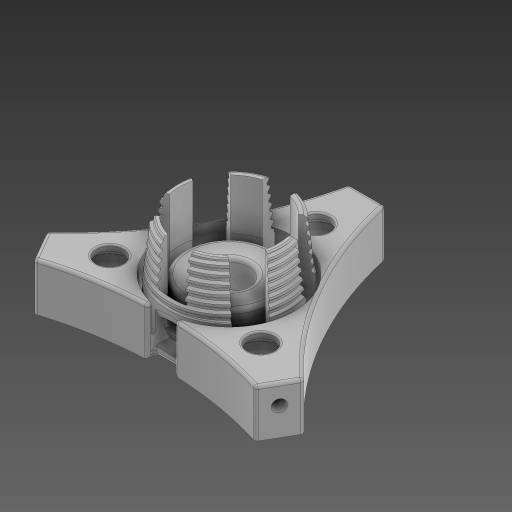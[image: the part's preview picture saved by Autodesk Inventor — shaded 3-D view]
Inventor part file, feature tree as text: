
AUTODESK INVENTOR PART (.ipt)
format: ipt  version: 2024 (Build 280153000, 153)  size: 1,730,560 bytes
history: native  units: mm
features: sketch x17, extrude x12, fillet x9, chamfer x3, hole x3, draft x2, helix x2, plane x2, pattern_circular x2, projected_geometry x2
ambient origin geometry x8: Origin, YZ Plane, XZ Plane, XY Plane, X Axis, Y Axis, Z Axis, Center Point
bodies: Solid1 (feature_tree)
feature tree (54):
  extrude  "Extrusion1"  Depth=29.5mm
  draft  "FaceDraft1"
  sketch  "Sketch2"  dims[d7=6.806784mm d8=0.55605mm]
  helix  "Coil1"  [1 undecoded]
  helix  "Coil2"  [1 undecoded]
  extrude  "Extrusion2"  Depth=0.55605mm
  extrude  "Extrusion3"  TaperAngle=0.0deg  [1 undecoded]
  fillet  "Fillet1"  [1 undecoded]
  chamfer  "Chamfer1"  Distance=0.3mm Angle=45.0deg
  plane  "Work Plane1"
  extrude  "Extrusion4"  TaperAngle=0.0deg  [1 undecoded]
  extrude  "Extrusion8"  Depth=60.0mm TaperAngle=360.0deg
  hole  "Hole2"  [1 undecoded]
  sketch  "Sketch13"  dims[d58=6.0mm d65=60.0mm d67=360.0deg]
  extrude  "Extrusion11"  Depth=10.0mm TaperAngle=0.0deg
  hole  "Bearing Hole"  [1 undecoded]
  pattern_circular  "Circular Pattern4"  Count=3 Angle=360.0deg
  extrude  "Extrusion13"  Depth=7.0mm TaperAngle=0.0deg
  sketch  "Sketch20"  dims[d126=6.804mm d127=6.0mm d128=9.979mm d129=8.89mm d130=90.0deg d131=8.0mm d132=20.594885mm d133=22.0mm d134=30.0mm d135=360.0deg]
  extrude  "Extrusion14"  Depth=1.55mm TaperAngle=45.0deg
  sketch  "Sketch18"  dims[d124=34.0mm]
  fillet  "Fillet9"  Radius=0.24mm
  chamfer  "Chamfer4"  [1 undecoded]
  chamfer  "Chamfer5"  Distance=0.5mm
  fillet  "Fillet11"  Radius=2.0mm
  draft  "FaceDraft2"
  fillet  "Fillet13"  Radius=34.767mm
  extrude  "Extrusion15"  Depth=0.5mm
  hole  "Hole5"  [1 undecoded]
  pattern_circular  "Circular Pattern5"  [2 undecoded]
  plane  "Work Plane4"
  extrude  "Extrusion16"  Depth=0.5mm
  fillet  "Fillet14"  Radius=30.0mm
  fillet  "Fillet16"  Radius=16.0mm
  extrude  "Extrusion17"  TaperAngle=0.0deg  [1 undecoded]
  extrude  "Extrusion19"  Depth=0.5mm
  fillet  "Fillet17"  Radius=0.4mm
  fillet  "Fillet18"  Radius=25.0mm
  fillet  "Fillet19"  Radius=22.0mm
  sketch  "Sketch1"  dims[d0=24.8mm d1=29.5mm d2=12.875mm d3=0.0mm d4=1.047198mm]
  projected_geometry  "Projected Loop1"
  sketch  "Sketch3"  dims[d9=6.806784mm]
  sketch  "Sketch4"  dims[d10=2.0mm d11=10.0mm d12=70.0mm d13=-1.047198mm d14=90.0deg d15=90.0deg d16=0.0mm d17=0.0mm d18=0.6mm]
  sketch  "Sketch5"  dims[d19=2.0mm d20=10.0mm d21=10.0mm d22=1.047198mm d23=90.0deg d24=90.0deg d25=0.0mm d26=0.0mm d27=0.0mm d28=0.0mm d29=0.0mm d30=0.0mm]
  sketch  "Sketch10"  dims[d31=0.6mm d32=0.3mm d33=2.0mm d34=45.0deg]
  sketch  "Sketch11"  dims[d36=-2.0mm d42=0.0mm d43=0.0mm]
  sketch  "Sketch15"  dims[d91=33.0mm d92=12.0mm d93=0.0mm]
  sketch  "Sketch17"  dims[d94=5.3mm d95=6.0mm d96=10.0mm d97=7.0mm d98=90.0deg d99=8.0mm d100=20.594885mm d122=10.0mm d123=0.0mm]
  sketch  "Sketch21"  dims[d146=11.34464mm d147=7.0mm d148=0.0mm]
  sketch  "Sketch22"  dims[d150=1.0mm d151=1.55mm d152=2.0mm d153=45.0deg]
  sketch  "Sketch25"  dims[d154=0.5mm d155=2.0mm d156=45.0deg d158=0.24mm]
  sketch  "Sketch26"  dims[d160=1.25mm d161=0.0mm d162=0.0mm]
  sketch  "Sketch28"  dims[d163=30.0deg d164=0.5mm d165=2.0mm d166=34.767mm d167=9.0mm d168=30.0deg d169=7.0mm d170=0.0mm d171=3.0mm d172=6.0mm d173=9.779mm d174=7.62mm d175=90.0deg d176=7.0mm d177=0.0mm d178=5.0mm d179=30.0mm d180=360.0deg d182=16.0mm d183=0.0mm d184=0.0mm d185=0.75mm d187=0.4mm d188=25.0mm d189=22.0mm d190=31.0mm d191=7.0mm d192=0.0mm d193=32.8mm d208=9.0mm d209=0.0mm d210=1.0mm d211=0.25mm d212=0.5mm d213=7.0mm d214=60.0mm d216=360.0deg]
  projected_geometry  "Project Cut Edges3"
note: 12 required parameter values undecoded (feature->parameter linkage not recoverable at this tier; creation-order binding heuristic only, values carry confidence <= 0.55)
